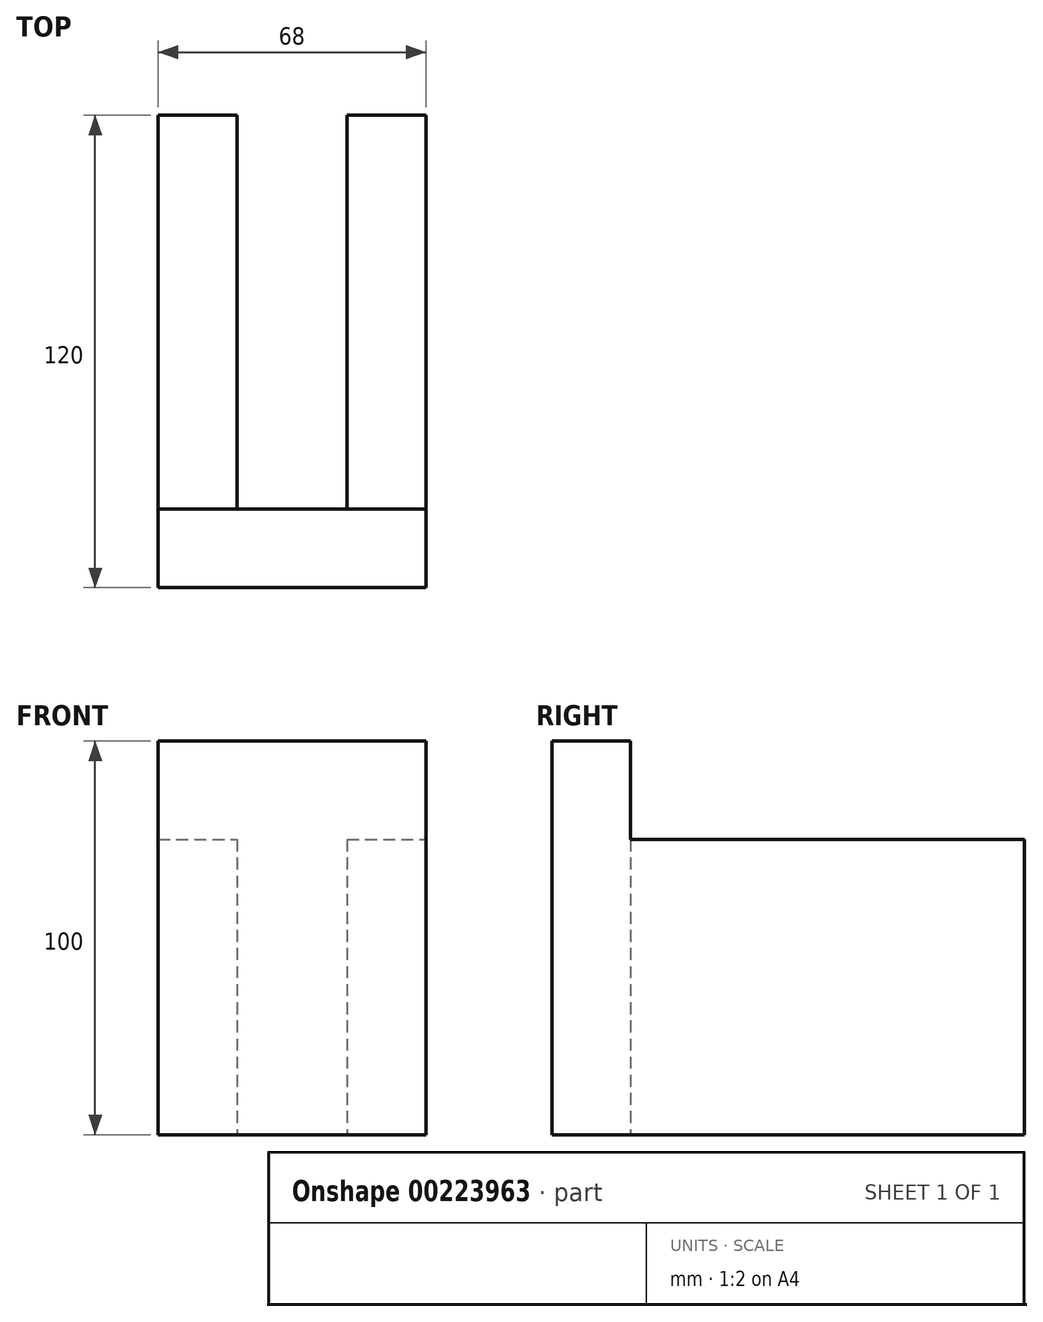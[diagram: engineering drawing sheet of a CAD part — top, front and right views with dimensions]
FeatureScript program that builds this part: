
annotation { "Feature Type Name" : "Feature", "Feature Type Description" : "" }
export const myFeature = defineFeature(function(context is Context, id is Id, definition is map)
    precondition{}
    {
        {
            var Q0;
            Q0=qCreatedBy(makeId("Top.planeOp"),FACE);
            var sketch = newSketch(context, id + "F0", { "sketchPlane" : qUnion([Q0])});
            skLineSegment(sketch, "E0.bottom", {"start": v(-133.35, -40) * mm, "end": v(-113.35, -40) * mm});
            skLineSegment(sketch, "E0.top", {"start": v(-133.35, 60) * mm, "end": v(-113.35, 60) * mm});
            skLineSegment(sketch, "E0.left", {"start": v(-133.35, -40) * mm, "end": v(-133.35, 60) * mm});
            skLineSegment(sketch, "E0.right", {"start": v(-113.35, -40) * mm, "end": v(-113.35, 60) * mm});
            skLineSegment(sketch, "E1.1.0.0", {"start": v(-65.35, -40) * mm, "end": v(-65.35, 60) * mm});
            skLineSegment(sketch, "E1.1.0.1", {"start": v(-85.35, 60) * mm, "end": v(-65.35, 60) * mm});
            skLineSegment(sketch, "E1.1.0.2", {"start": v(-85.35, -40) * mm, "end": v(-85.35, 60) * mm});
            skLineSegment(sketch, "E1.1.0.3", {"start": v(-85.35, -40) * mm, "end": v(-65.35, -40) * mm});
            skLineSegment(sketch, "E1.direction1", {"start": v(-133.35, -40) * mm, "end": v(-85.35, -40) * mm, "construction": true});
            skSolve(sketch);
        }
        {
            var Q0;
            Q0=qCreatedBy(makeId("Top.planeOp"),FACE);
            var sketch = newSketch(context, id + "F1", { "sketchPlane" : qUnion([Q0])});
            skLineSegment(sketch, "E2.bottom", {"start": v(-133.35, -40) * mm, "end": v(-65.35, -40) * mm});
            skLineSegment(sketch, "E2.top", {"start": v(-133.35, -60) * mm, "end": v(-65.35, -60) * mm});
            skLineSegment(sketch, "E2.left", {"start": v(-133.35, -40) * mm, "end": v(-133.35, -60) * mm});
            skLineSegment(sketch, "E2.right", {"start": v(-65.35, -40) * mm, "end": v(-65.35, -60) * mm});
            skSolve(sketch);
        }
        {
            var Q0;
            Q0=makeQuery(id+"F1.imprint","IMPRINT",FACE,{"disambiguationData":[TD([[makeQuery(id+"F1.imprint","IMPRINT",EDGE,{"derivedFrom":sQuery(id+"F1.wireOp",EDGE,"E2.bottom")}),-1.0]])]});
            extrude(context, id + "F2", {"entities" : qUnion([Q0]), "depth" : 100 * mm});
        }
        {
            var Q0;
            Q0=makeQuery(id+"F0.imprint","IMPRINT",FACE,{"disambiguationData":[TD([[makeQuery(id+"F0.imprint","IMPRINT",EDGE,{"derivedFrom":sQuery(id+"F0.wireOp",EDGE,"E0.bottom")}),1.0]])]});
            var Q1;
            Q1=makeQuery(id+"F0.imprint","IMPRINT",FACE,{"disambiguationData":[TD([[makeQuery(id+"F0.imprint","IMPRINT",EDGE,{"derivedFrom":sQuery(id+"F0.wireOp",EDGE,"E1.1.0.0")}),1.0]])]});
            extrude(context, id + "F3", {"entities" : qUnion([Q0, Q1]), "operationType" : NewBodyOperationType.ADD, "depth" : 75 * mm});
        }
    });
